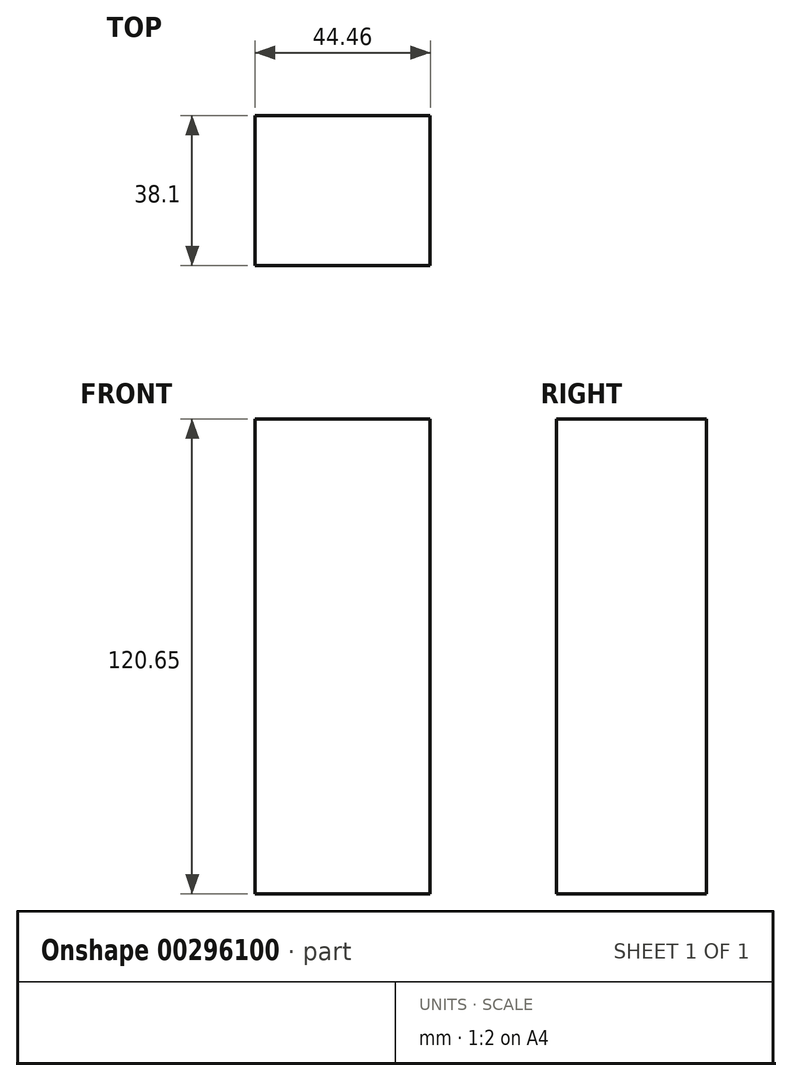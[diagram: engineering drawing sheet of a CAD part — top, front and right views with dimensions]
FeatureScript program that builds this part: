
annotation { "Feature Type Name" : "Feature", "Feature Type Description" : "" }
export const myFeature = defineFeature(function(context is Context, id is Id, definition is map)
    precondition{}
    {
        {
            var Q0;
            Q0=qCreatedBy(makeId("Top.planeOp"),FACE);
            var sketch = newSketch(context, id + "F0", { "sketchPlane" : qUnion([Q0])});
            skLineSegment(sketch, "E0.bottom", {"start": v(22.22, 19.05) * mm, "end": v(-22.23, 19.05) * mm});
            skLineSegment(sketch, "E0.top", {"start": v(22.23, -19.05) * mm, "end": v(-22.22, -19.05) * mm});
            skLineSegment(sketch, "E0.left", {"start": v(22.22, 19.05) * mm, "end": v(22.23, -19.05) * mm});
            skLineSegment(sketch, "E0.right", {"start": v(-22.23, 19.05) * mm, "end": v(-22.22, -19.05) * mm});
            skPoint(sketch, "E0.middle", {"position": v(0, 0) * mm});
            skSolve(sketch);
        }
        {
            var Q0;
            Q0=makeQuery(id+"F0.imprint","IMPRINT",FACE,{"disambiguationData":[TD([[makeQuery(id+"F0.imprint","IMPRINT",EDGE,{"derivedFrom":sQuery(id+"F0.wireOp",EDGE,"E0.bottom")}),1.0]])]});
            extrude(context, id + "F1", {"entities" : qUnion([Q0]), "depth" : 120.65 * mm});
        }
    });
